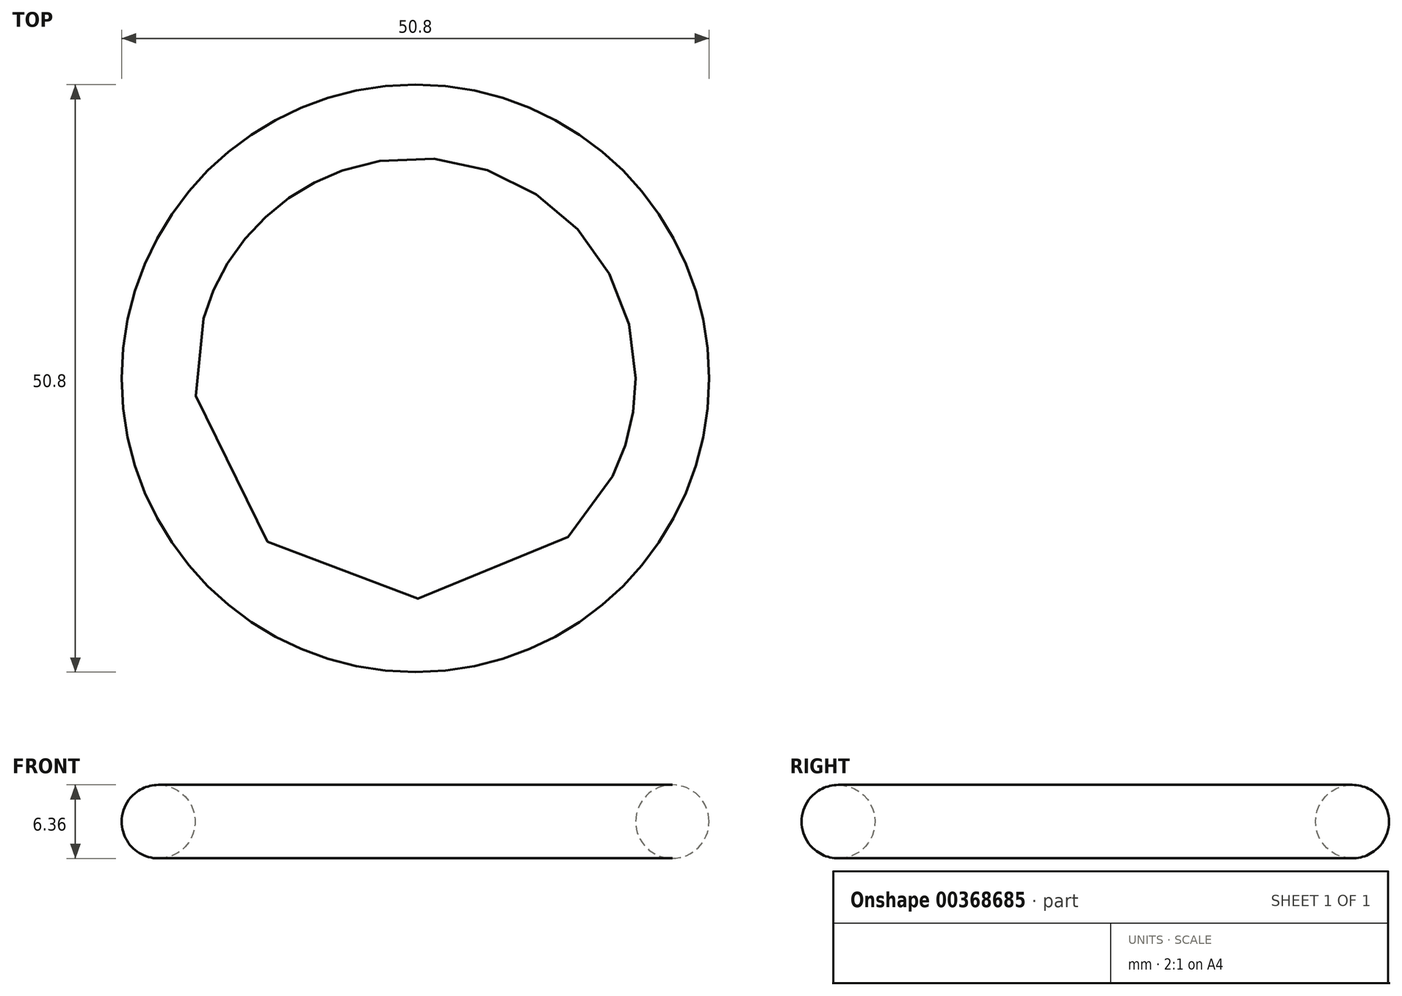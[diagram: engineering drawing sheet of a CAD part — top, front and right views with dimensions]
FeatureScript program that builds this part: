
annotation { "Feature Type Name" : "Feature", "Feature Type Description" : "" }
export const myFeature = defineFeature(function(context is Context, id is Id, definition is map)
    precondition{}
    {
        {
            var Q0;
            Q0=qCreatedBy(makeId("Front.planeOp"),FACE);
            var sketch = newSketch(context, id + "F0", { "sketchPlane" : qUnion([Q0])});
            skCircle(sketch, "E0", {"center": v(-22.23, 0) * mm, "radius": 3.18 * mm});
            skLineSegment(sketch, "E1", {"start": v(0, 12.54) * mm, "end": v(0, -8.2) * mm, "construction": true});
            skSolve(sketch);
        }
        {
            var Q0;
            Q0=qSketchRegion(id+"F0",true);
            var Q1;
            Q1=sQuery(id+"F0.wireOp",EDGE,"E1");
            revolve(context, id + "F1", {"entities" : qUnion([Q0]), "axis" : qUnion([Q1]), "revolveType" : RevolveType.FULL});
        }
    });
